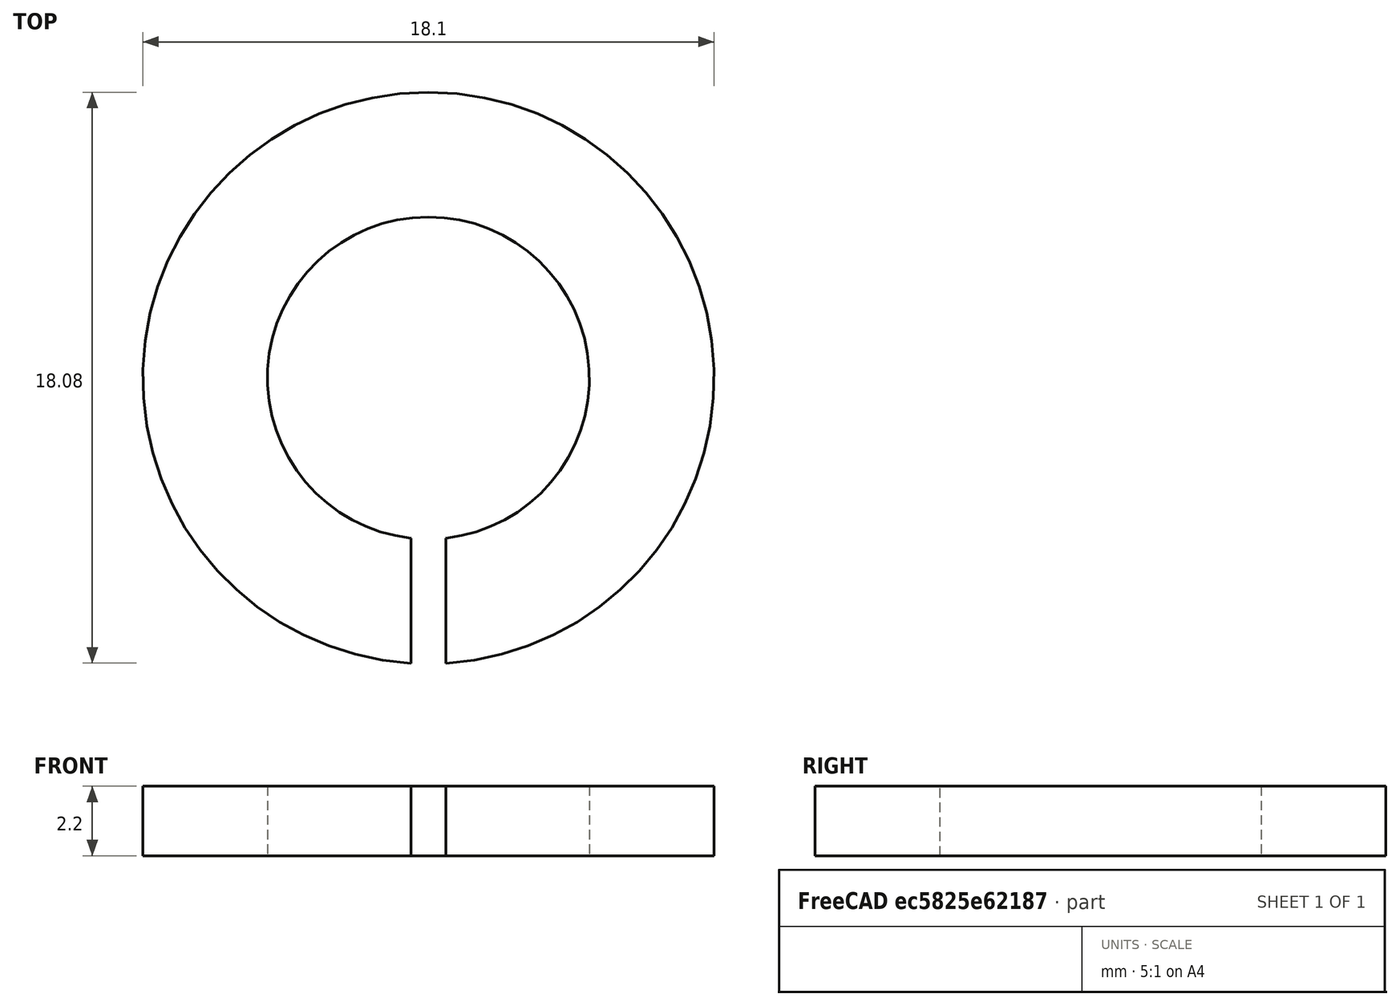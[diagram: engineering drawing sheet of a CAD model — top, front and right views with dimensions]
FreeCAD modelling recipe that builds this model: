
FCSTD DOCUMENT  (FreeCAD 0.15R4651 (Git))
Label: Federring_DIN127-B10
License: All rights reserved
LicenseURL: http://de.wikipedia.org/wiki/Alle_Rechte_vorbehalten
objects: Sketcher::SketchObject×1, PartDesign::Pad×1
note: 3 computed .brp shape members not serialized (recipe doc carries the construction recipe); baked Part::Feature solids carry a one-line shape summary decoded from their .brp

FEATURE [Sketcher::SketchObject] Sketch
  sketch-geometry (4):
    g0: ArcOfCircle CenterX=0 CenterY=0 CenterZ=0 NormalX=0 NormalY=0 NormalZ=1 Radius=5.1 StartAngle=4.82044 EndAngle=10.8875
    g1: ArcOfCircle CenterX=0 CenterY=0 CenterZ=0 NormalX=0 NormalY=0 NormalZ=1 Radius=9.05 StartAngle=4.7732 EndAngle=10.9348
    g2: LineSegment StartX=0.55 StartY=-5.07026 StartZ=0 EndX=0.55 EndY=-9.03327 EndZ=0
    g3: LineSegment StartX=-0.55 StartY=-9.03327 StartZ=0 EndX=-0.55 EndY=-5.07026 EndZ=0
  constraints (12):
    c: Coincident(g0,g-1)
    c: Coincident(g1,g-1)
    c: Vertical(g2)
    c: Vertical(g3)
    c: Coincident(g0,g2)
    c: Coincident(g0,g3)
    c: Coincident(g1,g2)
    c: Coincident(g1,g3)
    c: Symmetric(g1,g1,g-2)
    c: Radius(g0) = 5.1
    c: Radius(g1) = 9.05
    c: DistanceX(g1,g1) = -1.1
FEATURE [PartDesign::Pad] Pad  label="Federring DIN 127-B 10 #"
  Length = 2.2
  Length2 = 100
  Midplane = true
  Sketch = -> Sketch
  Type = 0
